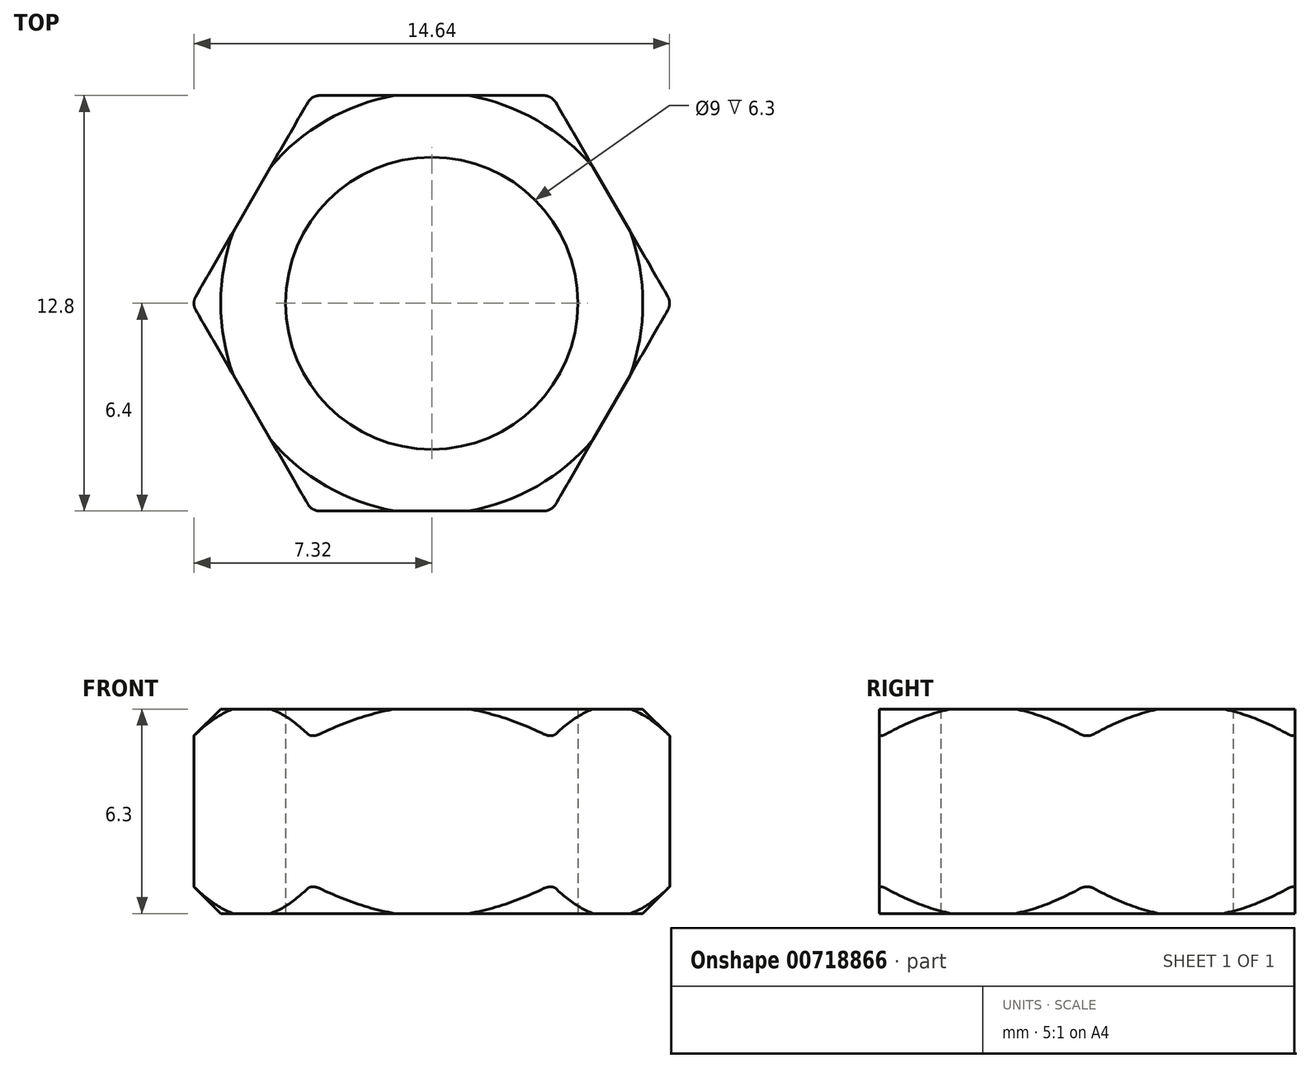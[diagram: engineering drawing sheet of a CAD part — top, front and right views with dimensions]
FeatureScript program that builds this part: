
annotation { "Feature Type Name" : "Feature", "Feature Type Description" : "" }
export const myFeature = defineFeature(function(context is Context, id is Id, definition is map)
    precondition{}
    {
        {
            var Q0;
            Q0=qCreatedBy(makeId("Top.planeOp"),FACE);
            var sketch = newSketch(context, id + "F0", { "sketchPlane" : qUnion([Q0])});
            skCircle(sketch, "E0.cCircle", {"center": v(0, 0) * mm, "radius": 6.4 * mm, "construction": true});
            skLineSegment(sketch, "E0.0", {"start": v(3.7, 6.4) * mm, "end": v(7.4, 0) * mm});
            skLineSegment(sketch, "E0.1", {"start": v(7.4, 0) * mm, "end": v(3.7, -6.4) * mm});
            skLineSegment(sketch, "E0.2", {"start": v(3.7, -6.4) * mm, "end": v(-3.7, -6.4) * mm});
            skLineSegment(sketch, "E0.3", {"start": v(-3.7, -6.4) * mm, "end": v(-7.4, 0) * mm});
            skLineSegment(sketch, "E0.4", {"start": v(-7.4, 0) * mm, "end": v(-3.7, 6.4) * mm});
            skLineSegment(sketch, "E0.5", {"start": v(-3.7, 6.4) * mm, "end": v(3.7, 6.4) * mm});
            skPoint(sketch, "E0.0.midPoint", {"position": v(5.54, 3.2) * mm});
            skSolve(sketch);
        }
        {
            var Q0;
            Q0 = qSketchRegion(id + "F0", true);
            extrude(context, id + "F1", {"entities" : qUnion([Q0]), "depth" : 6.3 * mm, "offsetDistance" : 25 * mm});
        }
        {
            var Q0;
            Q0=makeQuery(id+"F1.opExtrude","SWEPT_EDGE",EDGE,{"disambiguationData":[OSD([sQuery(id+"F0.wireOp",EDGE,"E0.2"),sQuery(id+"F0.wireOp",EDGE,"E0.3")])]});
            var Q1;
            Q1=makeQuery(id+"F1.opExtrude","SWEPT_EDGE",EDGE,{"disambiguationData":[OSD([sQuery(id+"F0.wireOp",EDGE,"E0.1"),sQuery(id+"F0.wireOp",EDGE,"E0.2")])]});
            var Q2;
            Q2=makeQuery(id+"F1.opExtrude","SWEPT_EDGE",EDGE,{"disambiguationData":[OSD([sQuery(id+"F0.wireOp",EDGE,"E0.0"),sQuery(id+"F0.wireOp",EDGE,"E0.1")])]});
            var Q3;
            Q3=makeQuery(id+"F1.opExtrude","SWEPT_EDGE",EDGE,{"disambiguationData":[OSD([sQuery(id+"F0.wireOp",EDGE,"E0.0"),sQuery(id+"F0.wireOp",EDGE,"E0.5")])]});
            var Q4;
            Q4=makeQuery(id+"F1.opExtrude","SWEPT_EDGE",EDGE,{"disambiguationData":[OSD([sQuery(id+"F0.wireOp",EDGE,"E0.4"),sQuery(id+"F0.wireOp",EDGE,"E0.5")])]});
            var Q5;
            Q5=makeQuery(id+"F1.opExtrude","SWEPT_EDGE",EDGE,{"disambiguationData":[OSD([sQuery(id+"F0.wireOp",EDGE,"E0.3"),sQuery(id+"F0.wireOp",EDGE,"E0.4")])]});
            fillet(context, id + "F2", {"entities" : qUnion([Q0, Q1, Q2, Q3, Q4, Q5]), "radius" : .4 * mm, "tangentPropagation" : true, "allowEdgeOverflow" : false});
        }
        {
            var Q0;
            Q0=qCreatedBy(makeId("Right.planeOp"),FACE);
            var sketch = newSketch(context, id + "F3", { "sketchPlane" : qUnion([Q0])});
            skLineSegment(sketch, "E1", {"start": v(6.5, 6.3) * mm, "end": v(9.5, 3.3) * mm});
            skLineSegment(sketch, "E2", {"start": v(9.5, 3.3) * mm, "end": v(9.5, 6.3) * mm});
            skLineSegment(sketch, "E3", {"start": v(9.5, 6.3) * mm, "end": v(6.5, 6.3) * mm});
            skLineSegment(sketch, "E4", {"start": v(0, 15.55) * mm, "end": v(0, 5.34) * mm});
            skLineSegment(sketch, "E5", {"start": v(-9.1, 3.15) * mm, "end": v(18.33, 3.15) * mm});
            skLineSegment(sketch, "E6.MirrorCS", {"start": v(6.5, 0) * mm, "end": v(9.5, 3) * mm});
            skLineSegment(sketch, "E7.MirrorCS", {"start": v(9.5, 0) * mm, "end": v(6.5, 0) * mm});
            skLineSegment(sketch, "E8.MirrorCS", {"start": v(9.5, 3) * mm, "end": v(9.5, 0) * mm});
            skSolve(sketch);
        }
        {
            var Q0;
            Q0=makeQuery(id+"F3.imprint","IMPRINT",FACE,{"disambiguationData":[TD([[makeQuery(id+"F3.imprint","IMPRINT",EDGE,{"derivedFrom":sQuery(id+"F3.wireOp",EDGE,"E1")}),1.0]])]});
            var Q1;
            Q1=makeQuery(id+"F3.imprint","IMPRINT",FACE,{"disambiguationData":[TD([[makeQuery(id+"F3.imprint","IMPRINT",EDGE,{"derivedFrom":sQuery(id+"F3.wireOp",EDGE,"E6.MirrorCS")}),-1.0]])]});
            var Q2;
            Q2=sQuery(id+"F3.wireOp",EDGE,"E4");
            revolve(context, id + "F4", {"operationType" : NewBodyOperationType.REMOVE, "surfaceOperationType" : NewSurfaceOperationType.NEW, "entities" : qUnion([Q0, Q1]), "axis" : qUnion([Q2]), "revolveType" : RevolveType.FULL});
        }
        {
            var Q0;
            Q0=sQuery(id+"F0.wireOp",VERTEX,"E0.cCircle.center");
            var Q1;
            Q1=makeQuery(id+"F1.opExtrude","SWEPT_BODY",BODY,{"disambiguationData":[OSD([sQuery(id+"F0.wireOp",EDGE,"E0.0"),sQuery(id+"F0.wireOp",EDGE,"E0.1"),sQuery(id+"F0.wireOp",EDGE,"E0.2"),sQuery(id+"F0.wireOp",EDGE,"E0.3"),sQuery(id+"F0.wireOp",EDGE,"E0.4"),sQuery(id+"F0.wireOp",EDGE,"E0.5")])]});
            hole(context, id + "F5", {"style" : HoleStyle.SIMPLE, "endStyle" : HoleEndStyle.THROUGH, "oppositeDirection" : true, "standardTappedOrClearance" : lookupTablePath({ "fit" : "Normal", "standard" : "ISO", "size" : "M8", "type" : "Clearance" }), "standardBlindInLast" : lookupTablePath({ "fit" : "Normal", "standard" : "ISO", "engagement" : "75%", "pitch" : "1.25 mm", "size" : "M8", "type" : "Clearance & tapped" }), "holeDiameter" : 9 * mm, "majorDiameter" : 5 * mm, "isTappedThrough" : true, "tappedDepth" : 12 * mm, "tapClearance" : 3, "locations" : qUnion([Q0]), "scope" : qUnion([Q1])});
        }
    });
